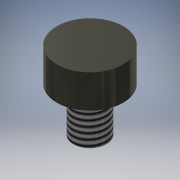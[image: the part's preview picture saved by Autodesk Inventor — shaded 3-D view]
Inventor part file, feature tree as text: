
AUTODESK INVENTOR PART (.ipt)
format: ipt  version: 2016 (Build 200138000, 138)  size: 124,416 bytes
history: native  units: mm
features: extrude x4, sketch x4, other x1, thread x1
ambient origin geometry x1: Origin
bodies: Body1 (feature_tree)
feature tree (10):
  other  "ソリッド1"
  extrude  "押し出し1"  Depth=3.0mm
  extrude  "押し出し2"  Depth=6.0mm TaperAngle=0.0deg
  thread  "ねじ1"
  extrude  "押し出し4"  Depth=6.0mm
  extrude  "押し出し5"  Depth=3.0mm TaperAngle=0.0deg
  sketch  "スケッチ1"
  sketch  "スケッチ2"
  sketch  "スケッチ4"
  sketch  "スケッチ5"
